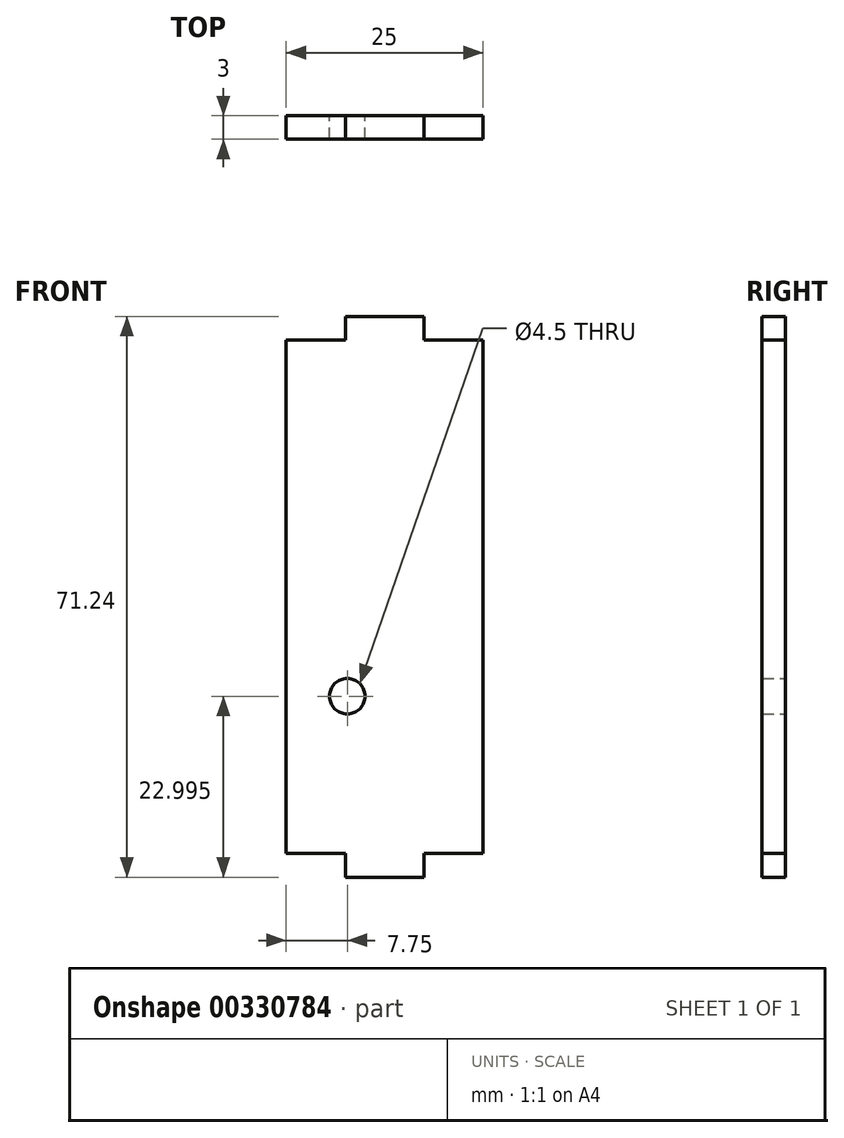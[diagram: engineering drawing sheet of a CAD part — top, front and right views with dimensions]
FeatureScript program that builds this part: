
annotation { "Feature Type Name" : "Feature", "Feature Type Description" : "" }
export const myFeature = defineFeature(function(context is Context, id is Id, definition is map)
    precondition{}
    {
        {
            var Q0;
            Q0=qCreatedBy(makeId("Front.planeOp"),FACE);
            var sketch = newSketch(context, id + "F0", { "sketchPlane" : qUnion([Q0])});
            skLineSegment(sketch, "E0.bottom", {"start": v(12.5, -32.62) * mm, "end": v(-12.5, -32.63) * mm});
            skLineSegment(sketch, "E0.top", {"start": v(12.5, 32.62) * mm, "end": v(-12.5, 32.62) * mm});
            skLineSegment(sketch, "E0.left", {"start": v(12.5, -32.62) * mm, "end": v(12.5, 32.62) * mm});
            skLineSegment(sketch, "E0.right", {"start": v(-12.5, -32.62) * mm, "end": v(-12.5, 32.62) * mm});
            skPoint(sketch, "E0.middle", {"position": v(0, 0) * mm});
            skLineSegment(sketch, "E1.bottom", {"start": v(-5, -32.62) * mm, "end": v(5, -32.62) * mm});
            skLineSegment(sketch, "E1.top", {"start": v(-5, -35.62) * mm, "end": v(5, -35.62) * mm});
            skLineSegment(sketch, "E1.left", {"start": v(-5, -32.62) * mm, "end": v(-5, -35.63) * mm});
            skLineSegment(sketch, "E1.right", {"start": v(5, -32.62) * mm, "end": v(5, -35.63) * mm});
            skLineSegment(sketch, "E2.bottom", {"start": v(-5, 32.62) * mm, "end": v(5, 32.62) * mm});
            skLineSegment(sketch, "E2.top", {"start": v(-5, 35.63) * mm, "end": v(5, 35.63) * mm});
            skLineSegment(sketch, "E2.left", {"start": v(-5, 32.62) * mm, "end": v(-5, 35.63) * mm});
            skLineSegment(sketch, "E2.right", {"start": v(5, 32.62) * mm, "end": v(5, 35.63) * mm});
            skCircle(sketch, "E3", {"center": v(-4.75, -12.63) * mm, "radius": 2.25 * mm});
            skSolve(sketch);
        }
        {
            var Q0;
            Q0 = qSketchRegion(id + "F0", true);
            extrude(context, id + "F1", {"entities" : qUnion([Q0]), "depth" : 3 * mm});
        }
    });
